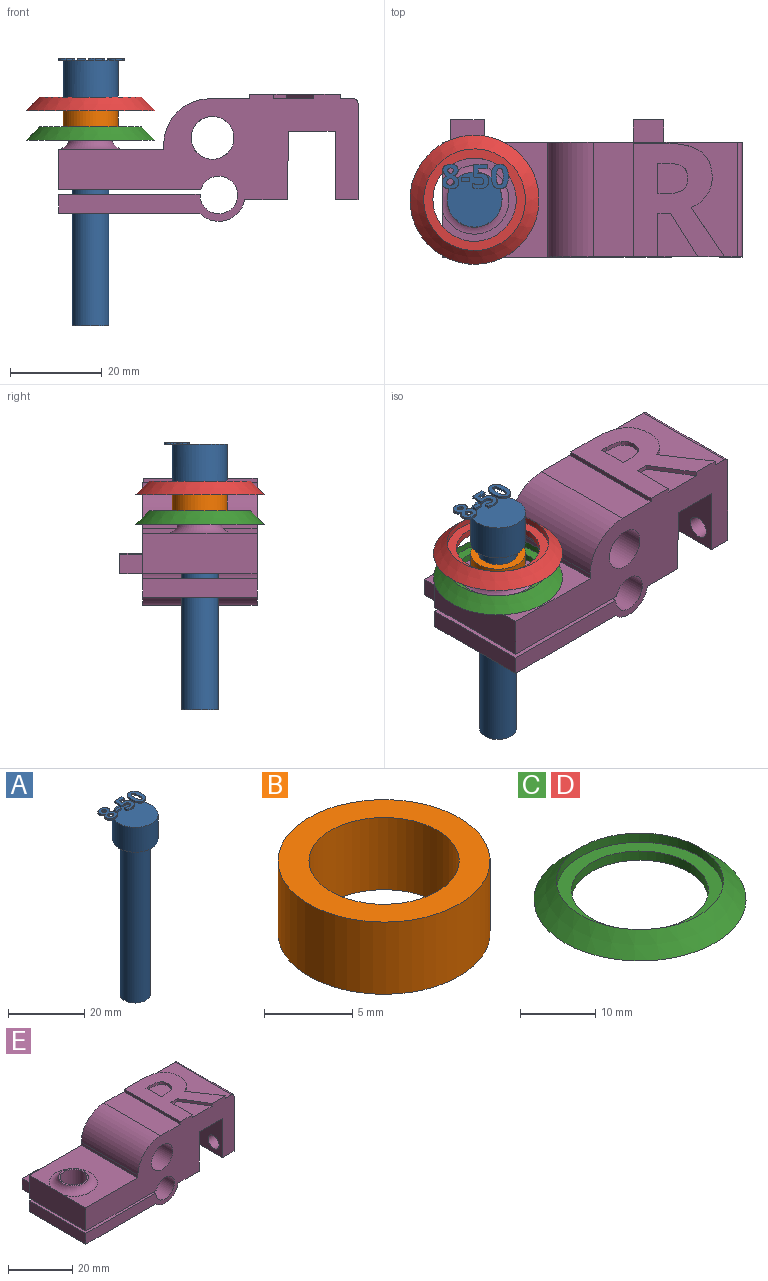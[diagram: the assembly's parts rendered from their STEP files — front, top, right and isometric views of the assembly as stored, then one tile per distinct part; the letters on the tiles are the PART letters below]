
ASSEMBLY  parts=5 mates=4
PART A: 86 faces, bbox 14.5x13.7x58.5 mm
  f0: plane 12x12mm, normal (0,0,1), area 99.4mm2, adj f5,f22,f23,f24,f25,f26,f40,f41
  f1: plane 1x0.26mm, normal (0,0,1), area 0.1mm2, adj f5,f46,f47,f48,f49
  f2: plane 0.85x0.68mm, normal (0,0,1), area 0.2mm2, adj f5,f29,f30,f31
  f3: cylinder r=4mm len=50mm, axis (0,0,-1), area 1256.6mm2, adj f4,f6
  f4: plane 8x8mm, normal (0,0,-1), area 50.3mm2, adj f3
  f5: cylinder r=6mm len=12mm, axis (0,0,-1), area 301.6mm2, adj f0,f1,f2,f6,f39,f45,f67,f85
  f6: plane 12x12mm, normal (0,0,-1), area 62.8mm2, adj f3,f5
  f7: extruded ~0.5x0.46mm, area 0.2mm2, adj f8,f37,f38,f39
  f8: extruded ~0.5x0.46mm, area 0.2mm2, adj f7,f9,f38,f39
  f9: extruded ~0.5x0.39mm, area 0.2mm2, adj f8,f10,f38,f39
  f10: extruded ~0.5x0.4mm, area 0.2mm2, adj f9,f11,f38,f39
  f11: extruded ~0.5x0.49mm, area 0.3mm2, adj f10,f12,f38,f39
  f12: extruded ~0.5x0.5mm, area 0.3mm2, adj f11,f13,f38,f39
  f13: extruded ~0.5x0.39mm, area 0.2mm2, adj f12,f37,f38,f39
  f14: extruded ~1.22x0.5mm, area 0.6mm2, adj f15,f35,f38,f39
  f15: extruded ~1.22x0.5mm, area 0.6mm2, adj f14,f16,f38,f39
  f16: extruded ~0.91x0.5mm, area 0.5mm2, adj f15,f17,f38,f39
  f17: extruded ~0.71x0.5mm, area 0.4mm2, adj f16,f18,f38,f39
  f18: extruded ~0.65x0.61mm, area 0.4mm2, adj f17,f19,f38,f39
  f19: extruded ~0.77x0.62mm, area 0.5mm2, adj f18,f20,f38,f39
  f20: extruded ~0.8x0.5mm, area 0.4mm2, adj f19,f21,f38,f39
  f21: extruded ~1.04x0.5mm, area 0.6mm2, adj f20,f22,f38,f39
  f22: extruded ~1.36x0.5mm, area 0.7mm2, adj f0,f21,f23,f38,f39
  f23: extruded ~1.33x0.5mm, area 0.7mm2, adj f0,f22,f24,f38
  f24: extruded ~1.04x0.51mm, area 0.6mm2, adj f0,f23,f25,f38
  f25: extruded ~0.75x0.5mm, area 0.4mm2, adj f0,f24,f26,f38
  f26: extruded ~0.85x0.66mm, area 0.5mm2, adj f0,f25,f27,f38,f39
  f27: extruded ~0.72x0.56mm, area 0.5mm2, adj f26,f28,f38,f39
  f28: extruded ~0.72x0.5mm, area 0.4mm2, adj f27,f35,f38,f39
  f29: extruded ~0.5x0.45mm, area 0.3mm2, adj f2,f30,f36,f38,f39
  f30: extruded ~0.5x0.47mm, area 0.3mm2, adj f2,f29,f31,f38
  f31: extruded ~0.62x0.5mm, area 0.3mm2, adj f2,f30,f32,f38,f39
  f32: extruded ~0.59x0.5mm, area 0.3mm2, adj f31,f33,f38,f39
  f33: extruded ~0.5x0.48mm, area 0.3mm2, adj f32,f34,f38,f39
  f34: extruded ~0.89x0.77mm, area 0.6mm2, adj f33,f36,f38,f39
  f35: extruded ~0.93x0.5mm, area 0.5mm2, adj f14,f28,f38,f39
  f36: extruded ~0.66x0.5mm, area 0.4mm2, adj f29,f34,f38,f39
  f37: extruded ~0.5x0.39mm, area 0.2mm2, adj f7,f13,f38,f39
  f38: plane 5.4x3.69mm, normal (0,0,1), area 12.7mm2, adj f7,f8,f9,f10,f11,f12,f13,f14
  f39: plane 5.4x3.53mm, normal (0,0,-1), area 10.2mm2, adj f5,f7,f8,f9,f10,f11,f12,f13
  f40: plane 0.9x0.5mm, normal (-1,0,0), area 0.4mm2, adj f0,f41,f43,f44
  f41: plane 1.93x0.5mm, normal (0,-1,0), area 1mm2, adj f0,f40,f42,f44
  f42: plane 0.9x0.5mm, normal (1,0,0), area 0.4mm2, adj f0,f41,f43,f44
  f43: plane 1.93x0.5mm, normal (0,1,0), area 1mm2, adj f0,f40,f42,f44
  f44: plane 1.93x0.9mm, normal (0,0,1), area 1.7mm2, adj f40,f41,f42,f43
  f45: plane 0.76x0.31mm, normal (0,0,-1), area 0mm2, adj f5,f46
  f46: extruded ~1.21x0.5mm, area 0.7mm2, adj f0,f1,f45,f47,f65,f66
  f47: extruded ~0.54x0.5mm, area 0.3mm2, adj f1,f46,f48,f66
  f48: plane 0.5x0.13mm, normal (-0.2,0.98,0), area 0.1mm2, adj f1,f47,f49,f66
  f49: plane 1.03x0.5mm, normal (1,-0.09,0), area 0.5mm2, adj f1,f48,f50,f66,f67
  f50: plane 1.88x0.5mm, normal (0,-1,0), area 0.9mm2, adj f49,f51,f66,f67
  f51: plane 0.94x0.5mm, normal (1,0,0), area 0.5mm2, adj f50,f52,f66,f67
  f52: plane 2.85x0.5mm, normal (0,1,0), area 1.4mm2, adj f51,f53,f66,f67
  f53: plane 2.68x0.5mm, normal (-1,0.07,0), area 1.3mm2, adj f0,f52,f54,f66,f67
  f54: plane 0.5x0.44mm, normal (-0.47,-0.88,0), area 0.3mm2, adj f0,f53,f55,f66
  f55: extruded ~0.5x0.37mm, area 0.2mm2, adj f0,f54,f56,f66
  f56: extruded ~0.5x0.42mm, area 0.2mm2, adj f0,f55,f57,f66
  f57: extruded ~1.05x0.8mm, area 0.8mm2, adj f0,f56,f58,f66
  f58: extruded ~1.02x0.83mm, area 0.8mm2, adj f0,f57,f59,f66
  f59: extruded ~0.72x0.5mm, area 0.4mm2, adj f0,f58,f60,f66
  f60: extruded ~0.66x0.5mm, area 0.4mm2, adj f0,f59,f61,f66
  f61: plane 0.96x0.5mm, normal (-1,0,0), area 0.5mm2, adj f0,f60,f62,f66
  f62: extruded ~1.42x0.5mm, area 0.7mm2, adj f0,f61,f63,f66
  f63: extruded ~1.55x0.5mm, area 0.8mm2, adj f0,f62,f64,f66
  f64: extruded ~1.36x0.54mm, area 0.8mm2, adj f0,f63,f65,f66
  f65: extruded ~1.17x0.5mm, area 0.6mm2, adj f0,f46,f64,f66
  f66: plane 5.33x3.51mm, normal (0,0,1), area 10.9mm2, adj f46,f47,f48,f49,f50,f51,f52,f53
  f67: plane 2.97x1.71mm, normal (0,0,-1), area 3.5mm2, adj f5,f49,f50,f51,f52,f53
  f68: extruded ~1.39x0.5mm, area 0.7mm2, adj f69,f83,f84,f85
  f69: extruded ~1.39x0.5mm, area 0.7mm2, adj f68,f70,f84,f85
  f70: extruded ~0.56x0.5mm, area 0.4mm2, adj f69,f71,f84,f85
  f71: extruded ~0.56x0.5mm, area 0.4mm2, adj f70,f72,f84,f85
  f72: extruded ~1.39x0.5mm, area 0.7mm2, adj f71,f73,f84,f85
  f73: extruded ~1.38x0.5mm, area 0.7mm2, adj f72,f74,f84,f85
  f74: extruded ~0.56x0.5mm, area 0.4mm2, adj f73,f83,f84,f85
  f75: extruded ~2.04x0.5mm, area 1.1mm2, adj f76,f82,f84,f85
  f76: extruded ~2.02x0.5mm, area 1.1mm2, adj f75,f77,f84,f85
  f77: extruded ~1.38x0.69mm, area 0.8mm2, adj f76,f78,f84,f85
  f78: extruded ~1.38x0.66mm, area 0.8mm2, adj f77,f79,f84,f85
  f79: extruded ~2.05x0.5mm, area 1.1mm2, adj f78,f80,f84,f85
  f80: extruded ~2.02x0.5mm, area 1mm2, adj f0,f79,f81,f84,f85
  f81: extruded ~1.37x0.68mm, area 0.8mm2, adj f0,f80,f82,f84
  f82: extruded ~1.39x0.66mm, area 0.8mm2, adj f0,f75,f81,f84,f85
  f83: extruded ~0.56x0.5mm, area 0.4mm2, adj f68,f74,f84,f85
  f84: plane 5.41x3.68mm, normal (0,0,1), area 12.1mm2, adj f68,f69,f70,f71,f72,f73,f74,f75
  f85: plane 5.41x3.68mm, normal (0,0,-1), area 10.3mm2, adj f5,f68,f69,f70,f71,f72,f73,f74
PART B: 4 faces, bbox 12x12x5 mm
  f0: cylinder r=4.25mm len=8.5mm, axis (0,0,-1), area 133.5mm2, adj f2,f3
  f1: cylinder r=6mm len=12mm, axis (0,0,-1), area 188.5mm2, adj f2,f3
  f2: plane 12x12mm, normal (0,0,1), area 56.4mm2, adj f0,f1
  f3: plane 12x12mm, normal (0,0,-1), area 56.4mm2, adj f0,f1
PART C: 5 faces, bbox 28.2x28.2x3 mm
  f0: cone r=11.1mm half-angle=45deg, axis (0,0,-1), area 335.9mm2, adj f1,f4
  f1: cylinder r=11.1mm len=22.2mm, axis (0,0,-1), area 104.6mm2, adj f0,f2
  f2: plane 22.2x22.2mm, normal (0,0,1), area 126.9mm2, adj f1,f3
  f3: cylinder r=9.1mm len=18.2mm, axis (0,0,-1), area 85.8mm2, adj f2,f4
  f4: plane 28.2x28.2mm, normal (0,0,-1), area 364.4mm2, adj f0,f3
PART D: same geometry as C
PART E: 56 faces, bbox 68.9x30x27.7 mm
  f0: plane 31.42x25mm, normal (0,0,1), area 392.1mm2, adj f14,f15,f25,f27,f40,f41,f42,f43
  f1: plane 9.51x8.71mm, normal (0,0,1), area 54.7mm2, adj f14,f37,f38,f39
  f2: plane 25x4.12mm, normal (-1,0,0), area 103mm2, adj f5,f14,f15,f19
  f3: cylinder r=4.17mm len=8.35mm, axis (0,0,1), area 108.1mm2, adj f5,f19
  f4: plane 25x9.34mm, normal (0,0,-1), area 233.4mm2, adj f13,f14,f15,f17
  f5: plane 30.88x25mm, normal (0,0,-1), area 717.2mm2, adj f2,f3,f14,f15,f17
  f6: plane 25x8.82mm, normal (-1,0,0), area 219.6mm2, adj f7,f14,f15,f20,f24
  f7: plane 25x23mm, normal (0,0,1), area 400mm2, adj f6,f8,f14,f15,f24
  f8: plane 25x1.1mm, normal (-1,0,0), area 27.5mm2, adj f7,f14,f15,f25
  f9: plane 25x21.09mm, normal (1,0,0), area 493.5mm2, adj f10,f14,f15,f22,f23,f27
  f10: plane 25x5mm, normal (0,0,-1), area 125mm2, adj f9,f11,f14,f15
  f11: plane 25x15mm, normal (-1,0,0), area 341.3mm2, adj f10,f12,f14,f15,f22,f23
  f12: plane 25x10.2mm, normal (0,0,-1), area 255mm2, adj f11,f13,f14,f15
  f13: plane 25x14.91mm, normal (1,0,-0.01), area 372.8mm2, adj f4,f12,f14,f15
  f14: plane 65.42x27.75mm, normal (0,-1,0), area 997.9mm2, adj f0,f1,f2,f4,f5,f6,f7,f8
  f15: plane 65.42x26.75mm, normal (0,1,0), area 926.8mm2, adj f0,f2,f4,f5,f6,f7,f8,f9
  f16: cylinder r=4.17mm len=10.78mm, axis (0,0,1), area 282.8mm2, adj f20,f21
  f17: cylinder r=5.75mm len=25mm, axis (0,-1,0), area 315.9mm2, adj f4,f5,f14,f15
  f18: cylinder r=4.1mm len=25mm, axis (0,-1,0), area 618.7mm2, adj f14,f15,f19,f20
  f19: plane 30.91x25mm, normal (0,0,1), area 718.1mm2, adj f2,f3,f14,f15,f18
  f20: plane 31.07x30mm, normal (0,0,-1), area 758.4mm2, adj f6,f14,f15,f16,f18,f29,f30,f31
  f21: plane 9.35x9.35mm, normal (0,0,1), area 13.9mm2, adj f16,f24
  f22: cylinder r=2.43mm len=5mm, axis (1,0,0), area 76.2mm2, adj f9,f11
  f23: cylinder r=2.2mm len=5mm, axis (1,0,0), area 69.1mm2, adj f9,f11
  f24: torus R=7.5mm, axis (0,0,-1), area 134.6mm2, adj f6,f7,f21
  f25: cylinder r=10mm len=25mm, axis (0,-1,0), area 392.7mm2, adj f0,f8,f14,f15
  f26: cylinder r=4.68mm len=25mm, axis (0,-1,0), area 735.2mm2, adj f14,f15
  f27: cylinder r=1mm len=25mm, axis (0,-1,0), area 39.3mm2, adj f0,f9,f14,f15
  f28: plane 7.3x5mm, normal (0,0,1), area 36.5mm2, adj f15,f29,f30,f31
  f29: plane 5x4.12mm, normal (-1,0,0), area 20.6mm2, adj f15,f20,f28,f31
  f30: plane 5x4.12mm, normal (1,0,0), area 20.6mm2, adj f15,f20,f28,f31
  f31: plane 7.3x4.12mm, normal (0,1,0), area 30.1mm2, adj f20,f28,f29,f30
  f32: plane 6.63x5mm, normal (0,0,1), area 33.2mm2, adj f15,f33,f35,f36
  f33: plane 5x4.5mm, normal (-1,0,0), area 22.5mm2, adj f15,f32,f34,f36
  f34: plane 6.63x5mm, normal (0,0,-1), area 33.2mm2, adj f15,f33,f35,f36
  f35: plane 5x4.5mm, normal (1,0,0), area 22.5mm2, adj f15,f32,f34,f36
  f36: plane 6.63x4.5mm, normal (0,1,0), area 29.9mm2, adj f32,f33,f34,f35
  f37: plane 9.51x1mm, normal (1,0,0), area 9.5mm2, adj f1,f14,f38,f54
  f38: plane 2.79x1mm, normal (0,-1,0), area 2.8mm2, adj f1,f37,f39,f54
  f39: plane 9.51x5.92mm, normal (-0.85,-0.53,0), area 11.2mm2, adj f1,f14,f38,f54
  f40: extruded ~10.8x7.29mm, area 13mm2, adj f0,f14,f41,f54
  f41: extruded ~3.41x2.67mm, area 4.4mm2, adj f0,f40,f42,f54
  f42: extruded ~3.89x1.2mm, area 4.1mm2, adj f0,f41,f43,f54
  f43: extruded ~5.59x2.42mm, area 6.3mm2, adj f0,f42,f44,f54
  f44: extruded ~7.48x1.84mm, area 7.8mm2, adj f0,f43,f45,f54
  f45: plane 7.22x1mm, normal (0,1,0), area 7.2mm2, adj f0,f44,f46,f54
  f46: plane 24.79x1mm, normal (-1,0,0), area 24.8mm2, adj f0,f14,f45,f54
  f47: plane 1.69x1mm, normal (0,1,0), area 1.7mm2, adj f48,f53,f54,f55
  f48: plane 6.7x1mm, normal (1,0,0), area 6.7mm2, adj f47,f49,f54,f55
  f49: plane 1.6x1mm, normal (0,-1,0), area 1.6mm2, adj f48,f50,f54,f55
  f50: extruded ~3.75x1mm, area 3.9mm2, adj f49,f51,f54,f55
  f51: extruded ~2.51x1.21mm, area 2.9mm2, adj f50,f52,f54,f55
  f52: extruded ~2.61x1.19mm, area 3mm2, adj f51,f53,f54,f55
  f53: extruded ~3.68x1mm, area 3.8mm2, adj f47,f52,f54,f55
  f54: plane 24.79x19.8mm, normal (0,0,1), area 300mm2, adj f14,f37,f38,f39,f40,f41,f42,f43
  f55: plane 6.7x6.56mm, normal (0,0,1), area 38.8mm2, adj f47,f48,f49,f50,f51,f52,f53
PLACE A t=(-103.78,-12.5,-28.71)mm
PLACE B rot(axis=(1,0,0),180deg) t=(-103.78,-12.5,18.29)mm
PLACE C t=(-103.78,-12.5,18.1)mm
PLACE D t=(-103.78,-12.5,24.6)mm
PLACE E t=(0,0,-1.11)mm
MATE fastened A.f3 <-> D.f0  axis (0,0,-1) through (-103.78,-12.5,21.29)mm
MATE fastened B.f0 <-> C.f0  axis (0,0,1) through (-103.78,-12.5,13.29)mm
MATE fastened C.f0 <-> E.f3  axis (0,0,-1) through (-103.78,-12.5,11.79)mm
MATE fastened D.f0 <-> B.f0  axis (0,0,-1) through (-103.78,-12.5,18.29)mm
